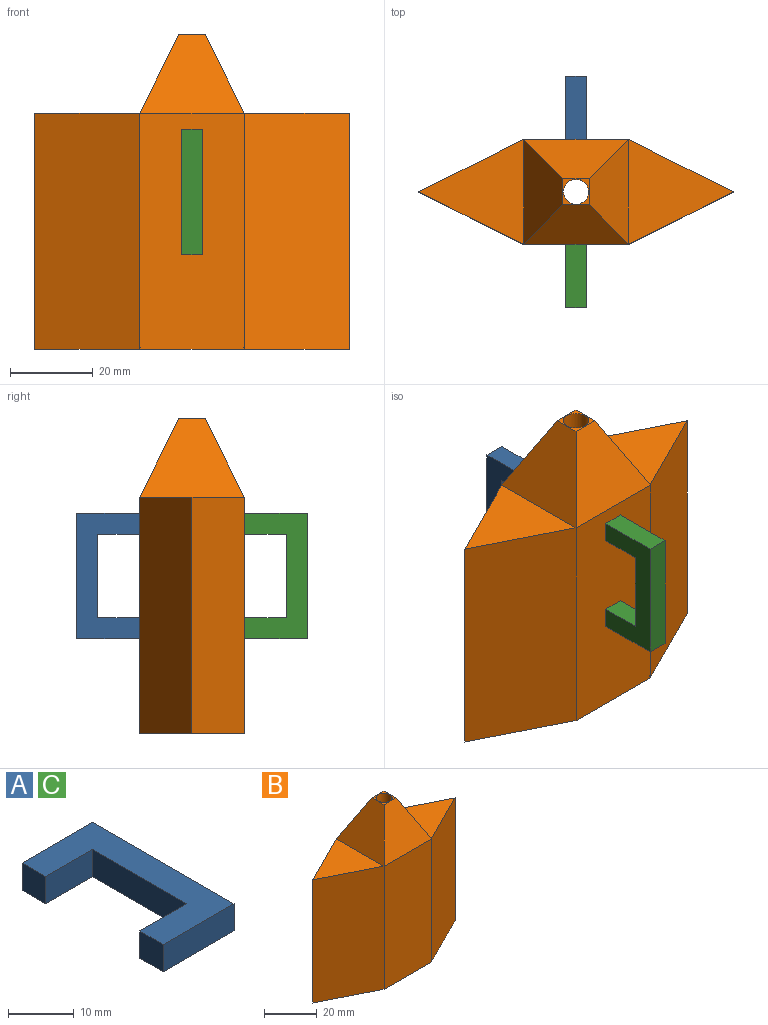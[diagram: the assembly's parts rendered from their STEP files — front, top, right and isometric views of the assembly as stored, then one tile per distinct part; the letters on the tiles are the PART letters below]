
ASSEMBLY  parts=3 mates=2
PART A: 10 faces, bbox 15.2x30.5x5.1 mm
  f0: plane 30.48x5.08mm, normal (1,0,0), area 154.8mm2, adj f1,f7,f8,f9
  f1: plane 15.24x5.08mm, normal (0,1,0), area 77.4mm2, adj f0,f2,f8,f9
  f2: plane 5.08x5.08mm, normal (-1,0,0), area 25.8mm2, adj f1,f3,f8,f9
  f3: plane 10.16x5.08mm, normal (0,-1,0), area 51.6mm2, adj f2,f4,f8,f9
  f4: plane 20.32x5.08mm, normal (-1,0,0), area 103.2mm2, adj f3,f5,f8,f9
  f5: plane 10.16x5.08mm, normal (0,1,0), area 51.6mm2, adj f4,f6,f8,f9
  f6: plane 5.08x5.08mm, normal (-1,0,0), area 25.8mm2, adj f5,f7,f8,f9
  f7: plane 15.24x5.08mm, normal (0,-1,0), area 77.4mm2, adj f0,f6,f8,f9
  f8: plane 30.48x15.24mm, normal (0,0,1), area 258.1mm2, adj f0,f1,f2,f3,f4,f5,f6,f7
  f9: plane 30.48x15.24mm, normal (0,0,-1), area 258.1mm2, adj f0,f1,f2,f3,f4,f5,f6,f7
PART B: 21 faces, bbox 76.2x25.4x76.2 mm
  f0: plane 25.4x25.4mm, normal (0,0,-1), area 322.6mm2, adj f13,f19,f20
  f1: plane 25.4x25.4mm, normal (0,0,1), area 322.6mm2, adj f9,f19,f20
  f2: plane 25.4x25.4mm, normal (0,0,1), area 322.6mm2, adj f10,f17,f18
  f3: plane 57.15x25.4mm, normal (0,1,0), area 1451.6mm2, adj f6,f12,f18,f19
  f4: plane 57.15x25.4mm, normal (0,-1,0), area 1451.6mm2, adj f7,f11,f17,f20
  f5: plane 6.35x6.35mm, normal (0,0,-1), area 11.1mm2, adj f6,f7,f13,f14,f16
  f6: plane 28.58x25.4mm, normal (0,-0.95,-0.32), area 478.2mm2, adj f3,f5,f13,f14
  f7: plane 28.58x25.4mm, normal (0,0.95,-0.32), area 478.2mm2, adj f4,f5,f13,f14
  f8: plane 6.35x6.35mm, normal (0,0,1), area 11.1mm2, adj f9,f10,f11,f12,f16
  f9: plane 25.4x19.05mm, normal (-0.89,0,0.45), area 338.1mm2, adj f1,f8,f11,f12
  f10: plane 25.4x19.05mm, normal (0.89,0,0.45), area 338.1mm2, adj f2,f8,f11,f12
  f11: plane 25.4x19.05mm, normal (0,-0.89,0.45), area 338.1mm2, adj f4,f8,f9,f10
  f12: plane 25.4x19.05mm, normal (0,0.89,0.45), area 338.1mm2, adj f3,f8,f9,f10
  f13: plane 28.58x25.4mm, normal (0.95,0,-0.32), area 478.2mm2, adj f0,f5,f6,f7
  f14: plane 28.58x25.4mm, normal (-0.95,0,-0.32), area 478.2mm2, adj f5,f6,f7,f15
  f15: plane 25.4x25.4mm, normal (0,0,-1), area 322.6mm2, adj f14,f17,f18
  f16: cylinder r=3.05mm len=47.63mm, axis (0,0,1), area 912.1mm2, adj f5,f8
  f17: plane 57.15x25.4mm, normal (0.45,-0.89,0), area 1622.9mm2, adj f2,f4,f15,f18
  f18: plane 57.15x25.4mm, normal (0.45,0.89,0), area 1622.9mm2, adj f2,f3,f15,f17
  f19: plane 57.15x25.4mm, normal (-0.45,0.89,0), area 1622.9mm2, adj f0,f1,f3,f20
  f20: plane 57.15x25.4mm, normal (-0.45,-0.89,0), area 1622.9mm2, adj f0,f1,f4,f19
PART C: same geometry as A
PLACE A rot(axis=(0.58,0.58,0.58),120deg) t=(-2.54,20.32,12.7)mm
PLACE B at identity fixed
PLACE C rot(axis=(0.58,-0.58,-0.58),120deg) t=(2.54,-20.32,12.7)mm
MATE fastened B.f3 <-> A.f2  axis (0,1,0) through (0,12.7,25.4)mm
MATE fastened C.f2 <-> B.f4  axis (0,1,0) through (0,-12.7,25.4)mm
